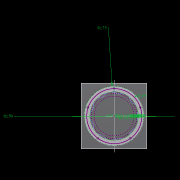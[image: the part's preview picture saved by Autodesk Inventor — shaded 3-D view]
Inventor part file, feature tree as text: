
AUTODESK INVENTOR PART (.ipt)
format: ipt  version: 2022.2 (Build 262287010, 287A)  size: 540,672 bytes
history: native  units: mm
features: other x19, extrude x19, sketch x12, pattern_circular x9, plane x3, fillet x2, move_body x2, revolve x2, draft x2, chamfer x2
ambient origin geometry x8: Origin, YZ Plane, XZ Plane, XY Plane, X Axis, Y Axis, Z Axis, Center Point
bodies: Solid5 (feature_tree)
feature tree (72):
  other  "CrossSection1"
  sketch  "Sketch7"  dims[d90=61.984365mm]
  other  "Roller1"
  other  "Roller2"
  sketch  "Sketch22"  dims[d167=8.972256mm]
  sketch  "Sketch2"  dims[d57=4.025mm]
  sketch  "Sketch23"  dims[d173=10.814812mm]
  other  "RevRoller1"
  fillet  "Fillet1"  Radius=59.246882mm
  pattern_circular  "Circular Pattern13"  Count=360  [1 undecoded]
  move_body  "Move Body7"
  revolve  "Revolution13"  [1 undecoded]
  fillet  "Fillet3"  Radius=0.025mm
  pattern_circular  "Circular Pattern14"  [2 undecoded]
  move_body  "Move Body6"
  revolve  "Revolution14"  [1 undecoded]
  other  "OuterRim_Top2"
  other  "OuterRim_Bottom2"
  plane  "Work Plane7"
  sketch  "Sketch47"  dims[d349=47.575591mm]
  sketch  "Sketch48"  dims[d350=47.575427mm]
  extrude  "Extrusion39"  Depth=5.596758mm
  extrude  "Extrusion40"  Depth=5.596758mm
  pattern_circular  "Circular Pattern28"  Angle=360.0deg  [1 undecoded]
  sketch  "Sketch49"  dims[d351=0.025mm d352=0.025mm d354=0.1mm d355=16.1595mm d356=16.159664mm d358=360.0deg d359=0.5mm d360=240.0mm d361=360.0deg d363=1.308997mm d367=8.1mm d370=0.1mm d371=1.0mm d372=1.308997mm d373=90.0deg d374=0.5mm d375=240.0mm d376=360.0deg d378=90.0deg d379=0.1mm d380=0.1mm d381=0.1mm d382=0.1mm d383=0.1mm d384=11.193516mm d385=0.0mm d386=0.0mm d391=50.0mm d392=75.0mm d393=1.5mm d394=1.5mm d395=1.5mm d396=1.5mm d397=90.0deg d398=90.0deg d399=90.0deg d400=75.0mm d401=11.193516mm d402=0.0mm d486=0.436332mm d487=0.5mm d488=2.0mm d489=0.0mm d490=20.0mm d495=2.5mm d496=8.0mm d506=13.856406mm d507=55.5mm d508=8.0mm d509=0.05mm d510=2.5mm d511=30.0deg d512=12.0mm d513=6.0mm d514=0.2mm d515=30.0deg d516=131.0mm d517=65.5mm d518=0.2mm d519=100.0mm d520=120.0mm d521=2.0mm d522=150.0mm d530=50.0mm d531=5.5mm d532=5.5mm d533=5.5mm d534=85.75mm d535=73.5mm d536=61.25mm d537=24.5mm d538=3.0mm d539=2.4mm d540=0.0mm d541=0.0mm d542=0.0mm d543=5.5mm d544=3.0mm d545=0.0mm d546=90.0mm d547=360.0deg d549=3.0mm d550=3.0mm d551=2.4mm d552=0.0mm d553=5.596758mm d554=0.0mm d555=2.4mm d556=0.0mm d557=5.596758mm d558=0.0mm d559=5.596758mm d560=0.0mm d561=90.0mm d562=360.0deg d564=60.0mm d565=360.0deg d567=5.5mm d568=5.5mm d569=3.0mm d570=0.0mm d571=5.596758mm d572=0.0mm d573=3.0mm d574=0.0mm d575=5.596758mm d576=0.0mm d577=90.0mm d578=360.0deg d580=60.0mm d581=360.0deg d584=20.0mm d585=8.0mm d587=1.75mm d589=3.0mm d592=2.0mm d593=12.0mm d594=12.0mm d600=0.5mm d601=2.0mm d602=45.0deg d603=0.5mm d604=2.0mm d605=45.0deg d606=0.436332mm d607=0.5mm d608=0.0mm d609=20.0mm d611=360.0deg d613=0.0mm d614=0.0mm d617=0.99971mm d618=100.0mm d620=69.0mm d621=3.0mm d622=5.5mm d623=5.596758mm d624=0.0mm d625=3.0mm d626=0.0mm d627=50.0mm d628=360.0deg d630=5.5mm d631=3.0mm d632=5.596758mm d633=0.0mm d634=2.593516mm d635=0.0mm d636=60.0mm d637=360.0deg d16=0.872665mm d17=0.872665mm d49=0.872665mm d50=0.872665mm d51=0.872665mm d52=0.872665mm d236=0.5mm d237=0.872665mm d238=0.5mm d239=0.872665mm d282=1.0mm d283=1.0mm d284=1.0mm d285=0.15mm d286=0.25mm d287=0.375mm d288=14.3117mm d289=0.75mm d290=20.594885mm d291=0.0625mm d292=0.75mm d293=0.375mm d405=0.5mm d406=0.872665mm d407=0.5mm d408=0.872665mm d413=0.5mm d414=0.872665mm d415=0.5mm d416=0.872665mm d417=0.5mm d418=0.872665mm d419=0.5mm d420=0.872665mm d421=0.872665mm d431=0.5mm d432=0.872665mm d433=0.5mm d434=0.872665mm d471=0.5mm d472=0.872665mm d473=0.5mm d474=0.872665mm d497=0.5mm d498=0.872665mm d499=0.5mm d500=0.872665mm d590=0.5mm d591=0.872665mm]
  extrude  "Extrusion41"  Depth=5.596758mm
  extrude  "Extrusion42"  Depth=5.596758mm
  pattern_circular  "Circular Pattern29"  Angle=360.0deg  [1 undecoded]
  extrude  "Rotor_Ring"  Depth=5.596758mm
  draft  "FaceDraft2"
  sketch  "Sketch30"  dims[d201=75.0mm d232=0.0mm d233=3600.0mm]
  plane  "Work Plane5"
  other  "Rotor Featurs"
  other  "RotorRim_Bottom"
  extrude  "Extrusion24"  Depth=5.596758mm
  extrude  "Extrusion25"  Depth=0.1mm
  extrude  "Extrusion26"  Depth=5.596758mm
  pattern_circular  "Circular Pattern23"  [2 undecoded]
  sketch  "Sketch41"  dims[d346=0.025mm]
  extrude  "Extrusion27"  TaperAngle=90.0deg  [1 undecoded]
  extrude  "Extrusion28"  Depth=5.596758mm
  pattern_circular  "Circular Pattern24"  Count=24  [1 undecoded]
  extrude  "Extrusion29"  TaperAngle=360.0deg  [1 undecoded]
  extrude  "Extrusion30"  TaperAngle=90.0deg  [1 undecoded]
  extrude  "Extrusion31"  Depth=0.1mm
  pattern_circular  "Circular Pattern25"  [2 undecoded]
  sketch  "Sketch42"  dims[d347=0.1mm]
  extrude  "Extrusion32"  Depth=0.1mm
  extrude  "Extrusion33"  Depth=0.1mm
  extrude  "Extrusion34"  Depth=0.1mm
  extrude  "Extrusion35"  Depth=5.596758mm
  pattern_circular  "Circular Pattern26"  [2 undecoded]
  pattern_circular  "Circular Pattern27"  [2 undecoded]
  chamfer  "Chamfer1"  Distance=50.0mm
  chamfer  "Chamfer2"  Distance=75.0mm
  draft  "FaceDraft4"
  plane  "Work Plane6"
  sketch  "Sketch43"  dims[d348=0.1mm]
  extrude  "Extrusion37"  Depth=1.5mm
  extrude  "Extrusion38"  Depth=1.5mm
  other  "2D Equation Curve1"
  sketch  "Sketch40"  dims[d343=16.1595mm d344=16.159664mm d345=0.025mm]
  other  "Work Axis6"
  other  "Work Axis7"
  other  "Work Axis8"
  other  "Work Axis9"
  other  "Work Axis10"
  other  "Work Point1"
  other  "Work Point2"
  other  "Work Point3"
  other  "Work Point4"
  other  "Work Point5"
note: 19 required parameter values undecoded (feature->parameter linkage not recoverable at this tier; creation-order binding heuristic only, values carry confidence <= 0.55)